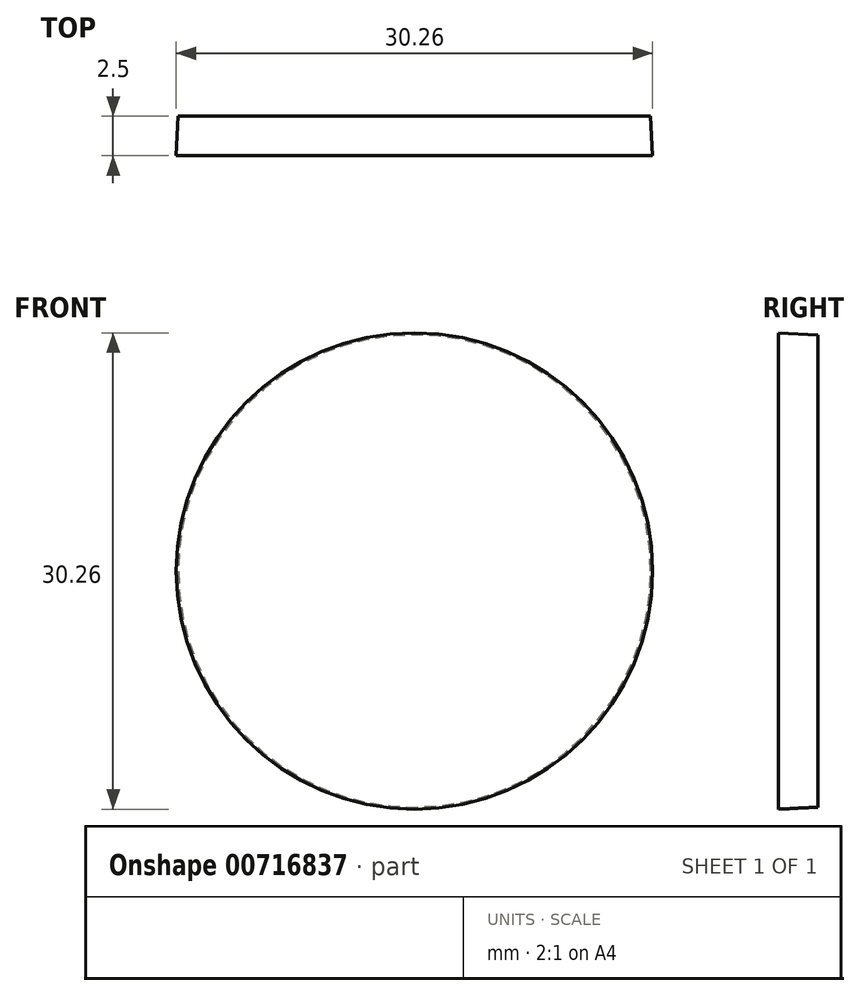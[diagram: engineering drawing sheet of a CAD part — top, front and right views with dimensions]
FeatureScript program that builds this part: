
annotation { "Feature Type Name" : "Feature", "Feature Type Description" : "" }
export const myFeature = defineFeature(function(context is Context, id is Id, definition is map)
    precondition{}
    {
        {
            var Q0;
            Q0=qCreatedBy(makeId("Front.planeOp"),FACE);
            var sketch = newSketch(context, id + "F0", { "sketchPlane" : qUnion([Q0])});
            skCircle(sketch, "E0", {"center": v(0, 0) * mm, "radius": 15 * mm});
            skSolve(sketch);
        }
        {
            var Q0;
            Q0=makeQuery(id+"F0.imprint","IMPRINT",FACE,{"disambiguationData":[TD([[makeQuery(id+"F0.imprint","IMPRINT",EDGE,{"derivedFrom":sQuery(id+"F0.wireOp",EDGE,"E0")}),1.0]])]});
            extrude(context, id + "F1", {"entities" : qUnion([Q0]), "depth" : 51.7 * mm, "offsetDistance" : 25 * mm, "hasDraft" : true, "draftAngle" : 3 * degree});
        }
        {
            var Q0;
            Q0=makeQuery(id+"F1.opExtrude","CAP_FACE",FACE,{"disambiguationData":[OSD([sQuery(id+"F0.wireOp",EDGE,"E0")])],"isStart":false});
            var Q1;
            Q1=makeQuery(id+"F1.opExtrude","SWEPT_FACE",FACE,{"disambiguationData":[OSD([sQuery(id+"F0.wireOp",EDGE,"E0")])]});
            shell(context, id + "F2", {"entities" : qUnion([Q0, Q1]), "thickness" : 2.5 * mm});
        }
    });
